# Revit family: Hager-UNIVERS-Surface_mounted-IP44-With_Cover-Without_DIN-Hosted-NL-en
name_source: partatom
category: Electrical Equipment
units: mm (PartAtom-declared; Revit-internal decimal feet)

## family parameters
Cut with Voids When Loaded = No
Host = Face
Maintain Annotation Orientation = Yes
Panel Configuration = Two Columns, Circuits Across
Part Type = Panelboard
Room Calculation Point = No
Round Connector Dimension = Use Diameter
Shared = No

## types (28) — shared parameters
BC_MODEL_ID = 1546903
BC_OBJECT_ID = 513403
BC_OBJECT_VERSION = #4
Code hager = ADD-EC000214_EU
EF000003 - Mounting method = Surface mounted
EF000007 - Colour = White
EF000024 - UV resistant = No
EF000049 - Depth = 161 mm  [stored 0.528215 ft]
EF000116 - RAL-number = 9010
EF000118 - With mounting plate = No
EF001062 - EMC-version = No
EF001088 - Extension possible = Yes
EF001134 - DIN-rail = No
EF004462 - Type of closure = Other
EF005474 - Degree of protection (IP) = IP44
EF006244 - Transparent cover/door = No
EF006306 - With lock = No
EF009212 - Cover model = With notch
EF015776 - Earthing terminal block = No
EF015777 - Neutral terminal block = No
EF015941 - Signal passing door = No
ETIM class code = EC000214
ETIM class name = Small distribution board
HG000002-With door or cover = Yes
HG000003-Range = UNIVERS
HG000005-Thickness = 2 mm  [stored 0.00656168 ft]
HG000006-Flush mounted = No
HG000011-Empty rows from bottom = No
HG000012-Door swing angle = 90.00°
HG000013-Door on the left = No
HG000014-Door on the right = Yes
HG000015-Clearance visibility = Yes
HG000016-Door 3D visibility = Yes
HG000017-Distance between poles = 18 mm  [stored 0.0590551 ft]
HG000060-RAL-number = 9010
HG000099-Onfly Template ID = 507532
Manufacturer = Hager
Name = UNIVERS-Surface_mounted-IP44-With_Cover-Without_DIN-NL
Name BIM&CO = Electricity
Name hager = ADD_Enclosures_EC000214
Uniformat = Low Tension Service & Dist.
Uniformat code = D501001
zero-valued in all types: Default Elevation, EF001131 - Inner depth, HG000007-Number of empty columns

## per-type parameters (varying)
| type | BC_VARIANT_ID | EF000008 - Width | EF000040 - Height | EF000218 - Built-in depth | EF000266 - Number of rows | EF000332 - Built-in height | EF000846 - Built-in width | EF002950 - Width in number of modular spacings | HG000001-Number of columns | HG000004-Manufacturer reference | HG000008-Number of empty rows | HG000009-Double swing door | HG000010-Asymmetric doors | HGEF000266-Number of rows | HGEF002950-Width in number of modular spacings |
| UNIVERS-Surface_mounted_W300_H500_D161_12_Modular_Spacing-FWQ31P | 1173250 | 300 mm | 500 mm  [stored 1.64042 ft] | 0 mm  [stored 0 ft] | 3 | 500 mm  [stored 1.64042 ft] | 300 mm | 12 | 1 | FWQ31P | 0 | No | No | 3 | 12 |
| UNIVERS-Surface_mounted_W550_H500_D161_24_Modular_Spacing-FWQ32P | 1173251 | 550 mm | 500 mm  [stored 1.64042 ft] | 161 mm  [stored 0.528215 ft] | 3 | 500 mm  [stored 1.64042 ft] | 550 mm | 24 | 2 | FWQ32P | 0 | No | No | 3 | 24 |
| UNIVERS-Surface_mounted_W800_H500_D161_36_Modular_Spacing-FWQ33P | 1173252 | 800 mm  [stored 2.62467 ft] | 500 mm  [stored 1.64042 ft] | 0 mm  [stored 0 ft] | 3 | 500 mm  [stored 1.64042 ft] | 800 mm  [stored 2.62467 ft] | 36 | 3 | FWQ33P | 0 | Yes | Yes | 3 | 36 |
| UNIVERS-Surface_mounted_W1050_H500_D161_48_Modular_Spacing-FWQ34P | 1173253 | 1050 mm | 500 mm  [stored 1.64042 ft] | 0 mm  [stored 0 ft] | 3 | 500 mm  [stored 1.64042 ft] | 1050 mm | 48 | 4 | FWQ34P | 0 | Yes | No | 3 | 48 |
| UNIVERS-Surface_mounted_W300_H650_D161_12_Modular_Spacing-FWQ41P | 1173254 | 300 mm | 650 mm  [stored 2.13255 ft] | 0 mm  [stored 0 ft] | 4 | 650 mm  [stored 2.13255 ft] | 300 mm | 12 | 1 | FWQ41P | 0 | No | No | 4 | 12 |
| UNIVERS-Surface_mounted_W550_H650_D161_24_Modular_Spacing-FWQ42P | 1173255 | 550 mm | 650 mm  [stored 2.13255 ft] | 0 mm  [stored 0 ft] | 4 | 650 mm  [stored 2.13255 ft] | 550 mm | 24 | 2 | FWQ42P | 0 | No | No | 4 | 24 |
| UNIVERS-Surface_mounted_W800_H650_D161_36_Modular_Spacing-FWQ43P | 1173256 | 800 mm  [stored 2.62467 ft] | 650 mm  [stored 2.13255 ft] | 0 mm  [stored 0 ft] | 4 | 650 mm  [stored 2.13255 ft] | 800 mm  [stored 2.62467 ft] | 36 | 3 | FWQ43P | 0 | Yes | Yes | 4 | 36 |
| UNIVERS-Surface_mounted_W1050_H650_D161_48_Modular_Spacing-FWQ44P | 1173257 | 1050 mm | 650 mm  [stored 2.13255 ft] | 0 mm  [stored 0 ft] | 4 | 650 mm  [stored 2.13255 ft] | 1050 mm | 48 | 4 | FWQ44P | 0 | Yes | No | 4 | 48 |
| UNIVERS-Surface_mounted_W300_H800_D161_12_Modular_Spacing-FWQ51P | 1173258 | 300 mm | 800 mm  [stored 2.62467 ft] | 0 mm  [stored 0 ft] | 5 | 800 mm  [stored 2.62467 ft] | 300 mm | 12 | 1 | FWQ51P | 0 | No | No | 5 | 12 |
| UNIVERS-Surface_mounted_W550_H800_D161_24_Modular_Spacing-FWQ52N | 1173259 | 550 mm | 800 mm  [stored 2.62467 ft] | 0 mm  [stored 0 ft] | 5 | 800 mm  [stored 2.62467 ft] | 550 mm | 24 | 2 | FWQ52N | 2 | No | No | 5 | 24 |
| UNIVERS-Surface_mounted_W550_H800_D161_24_Modular_Spacing-FWQ52P | 1173260 | 550 mm | 800 mm  [stored 2.62467 ft] | 161 mm  [stored 0.528215 ft] | 5 | 800 mm  [stored 2.62467 ft] | 550 mm | 24 | 2 | FWQ52P | 0 | No | No | 5 | 24 |
| UNIVERS-Surface_mounted_W800_H800_D161_36_Modular_Spacing-FWQ53N | 1173261 | 800 mm  [stored 2.62467 ft] | 800 mm  [stored 2.62467 ft] | 161 mm  [stored 0.528215 ft] | 5 | 800 mm  [stored 2.62467 ft] | 800 mm  [stored 2.62467 ft] | 36 | 3 | FWQ53N | 2 | Yes | Yes | 5 | 36 |
| UNIVERS-Surface_mounted_W800_H800_D161_36_Modular_Spacing-FWQ53P | 1173262 | 800 mm  [stored 2.62467 ft] | 800 mm  [stored 2.62467 ft] | 0 mm  [stored 0 ft] | 5 | 800 mm  [stored 2.62467 ft] | 800 mm  [stored 2.62467 ft] | 36 | 3 | FWQ53P | 0 | Yes | Yes | 5 | 36 |
| UNIVERS-Surface_mounted_W1050_H800_D161_48_Modular_Spacing-FWQ54P | 1173263 | 1050 mm | 800 mm  [stored 2.62467 ft] | 0 mm  [stored 0 ft] | 5 | 800 mm  [stored 2.62467 ft] | 1050 mm | 48 | 4 | FWQ54P | 0 | Yes | No | 5 | 48 |
| UNIVERS-Surface_mounted_W300_H950_D161_12_Modular_Spacing-FWQ61P | 1173264 | 300 mm | 950 mm  [stored 3.1168 ft] | 0 mm  [stored 0 ft] | 6 | 950 mm  [stored 3.1168 ft] | 300 mm | 12 | 1 | FWQ61P | 0 | No | No | 6 | 12 |
| UNIVERS-Surface_mounted_W550_H950_D161_24_Modular_Spacing-FWQ62N | 1173265 | 550 mm | 950 mm  [stored 3.1168 ft] | 0 mm  [stored 0 ft] | 6 | 950 mm  [stored 3.1168 ft] | 550 mm | 24 | 2 | FWQ62N | 2 | No | No | 6 | 24 |
| UNIVERS-Surface_mounted_W550_H950_D161_24_Modular_Spacing-FWQ62P | 1173266 | 550 mm | 950 mm  [stored 3.1168 ft] | 161 mm  [stored 0.528215 ft] | 6 | 950 mm  [stored 3.1168 ft] | 550 mm | 24 | 2 | FWQ62P | 0 | No | No | 6 | 24 |
| UNIVERS-Surface_mounted_W800_H950_D161_36_Modular_Spacing-FWQ63N | 1173267 | 800 mm  [stored 2.62467 ft] | 950 mm  [stored 3.1168 ft] | 161 mm  [stored 0.528215 ft] | 6 | 950 mm  [stored 3.1168 ft] | 800 mm  [stored 2.62467 ft] | 36 | 3 | FWQ63N | 2 | Yes | Yes | 6 | 36 |
| UNIVERS-Surface_mounted_W800_H950_D161_36_Modular_Spacing-FWQ63P | 1173268 | 800 mm  [stored 2.62467 ft] | 950 mm  [stored 3.1168 ft] | 0 mm  [stored 0 ft] | 6 | 950 mm  [stored 3.1168 ft] | 800 mm  [stored 2.62467 ft] | 36 | 3 | FWQ63P | 0 | Yes | Yes | 6 | 36 |
| UNIVERS-Surface_mounted_W1050_H950_D161_48_Modular_Spacing-FWQ64N | 1173269 | 1050 mm | 950 mm  [stored 3.1168 ft] | 0 mm  [stored 0 ft] | 6 | 950 mm  [stored 3.1168 ft] | 1050 mm | 48 | 4 | FWQ64N | 2 | Yes | No | 6 | 48 |
| UNIVERS-Surface_mounted_W1050_H950_D161_48_Modular_Spacing-FWQ64P | 1173270 | 1050 mm | 950 mm  [stored 3.1168 ft] | 161 mm  [stored 0.528215 ft] | 6 | 950 mm  [stored 3.1168 ft] | 1050 mm | 48 | 4 | FWQ64P | 0 | Yes | No | 6 | 48 |
| UNIVERS-Surface_mounted_W300_H1100_D161_12_Modular_Spacing-FWQ71P | 1173271 | 300 mm | 1100 mm  [stored 3.60892 ft] | 161 mm  [stored 0.528215 ft] | 7 | 1100 mm  [stored 3.60892 ft] | 300 mm | 12 | 1 | FWQ71P | 0 | No | No | 7 | 12 |
| UNIVERS-Surface_mounted_W550_H1100_D161_24_Modular_Spacing-FWQ72N | 1173272 | 550 mm | 1100 mm  [stored 3.60892 ft] | 161 mm  [stored 0.528215 ft] | 7 | 1100 mm  [stored 3.60892 ft] | 550 mm | 24 | 2 | FWQ72N | 2 | No | No | 7 | 24 |
| UNIVERS-Surface_mounted_W550_H1100_D161_12_Modular_Spacing-FWQ72P | 1173273 | 550 mm | 1100 mm  [stored 3.60892 ft] | 0 mm  [stored 0 ft] | 7 | 1100 mm  [stored 3.60892 ft] | 550 mm | 12 | 2 | FWQ72P | 0 | No | No | 7 | 12 |
| UNIVERS-Surface_mounted_W800_H1100_D161_36_Modular_Spacing-FWQ73N | 1173274 | 800 mm  [stored 2.62467 ft] | 1100 mm  [stored 3.60892 ft] | 0 mm  [stored 0 ft] | 7 | 1100 mm  [stored 3.60892 ft] | 800 mm  [stored 2.62467 ft] | 36 | 3 | FWQ73N | 2 | Yes | Yes | 7 | 36 |
| UNIVERS-Surface_mounted_W800_H1100_D161_12_Modular_Spacing-FWQ73P | 1173275 | 800 mm  [stored 2.62467 ft] | 1100 mm  [stored 3.60892 ft] | 161 mm  [stored 0.528215 ft] | 7 | 1100 mm  [stored 3.60892 ft] | 800 mm  [stored 2.62467 ft] | 12 | 3 | FWQ73P | 0 | Yes | Yes | 7 | 12 |
| UNIVERS-Surface_mounted_W1050_H1100_D161_48_Modular_Spacing-FWQ74N | 1173276 | 1050 mm | 1100 mm  [stored 3.60892 ft] | 161 mm  [stored 0.528215 ft] | 7 | 1100 mm  [stored 3.60892 ft] | 1050 mm | 48 | 4 | FWQ74N | 2 | Yes | No | 7 | 48 |
| UNIVERS-Surface_mounted_W1050_H1100_D161_12_Modular_Spacing-FWQ74P | 1173277 | 1050 mm | 1100 mm  [stored 3.60892 ft] | 161 mm  [stored 0.528215 ft] | 7 | 1100 mm  [stored 3.60892 ft] | 1050 mm | 12 | 4 | FWQ74P | 0 | Yes | No | 7 | 12 |

note: column(s) folded — value = type name in every type: Reference

note: [stored X ft] marks values corroborated as IEEE doubles in the binary element streams (Revit-internal decimal feet)

## geometry (parser evidence)
native form markers: Sweep x17
no freeform markers — native parametric forms only
